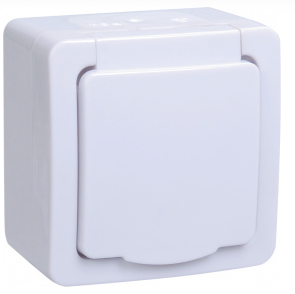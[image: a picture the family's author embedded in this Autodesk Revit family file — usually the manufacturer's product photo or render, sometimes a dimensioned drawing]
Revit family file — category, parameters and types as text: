
# Revit family: IEK_Розетка_ОУ_сЗК_сКР_16А_1мст_IP54_ГЕРМЕС_PLUS_белый
name_source: partatom
category: Электрические приборы
units: mm (PartAtom-declared; Revit-internal decimal feet)

## family parameters
Всегда вертикально = Да
На основе рабочей плоскости = Нет
Общий = Нет
При загрузке вырезать с полостями = Нет
Размер круглого соединителя = Использовать диаметр
Сохранять ориентацию аннотаций = Да
Тип детали = Нормальный
Точка расчета площади = Нет

## types (2) — shared parameters
ADSK_URL страницы изделия = https://qr.iek.group
ADSK_Версия Revit = v2019
ADSK_Версия семейства = 01.10.25
ADSK_Группирование = Электроустановочные изделия низковольтные
ADSK_Единица измерения = шт.
ADSK_Завод-изготовитель = IEK
ADSK_Количество фаз = 1
ADSK_Количество фаз числовое = 1
ADSK_Марка = ГЕРМЕС PLUS
ADSK_Материал = Цвет белый
ADSK_Материал наименование = Пластик
ADSK_Напряжение = 220 В
URL = https://www.iek.ru
Высота = 72 мм
Глубина = 52 мм
Изготовитель = IEK
Описание = Изделия серии "ГЕРМЕС PLUS" используются в помещениях с повышенной влажностью или запыленностью, а также под навесом на открытом воздухе.
Степень защиты = IP54
Тип монтажа = Поверхность монтажа (открытая установка)
Ширина = 72 мм

## per-type parameters (varying)
| type | ADSK_Код изделия | ADSK_Масса | ADSK_Наименование | ADSK_Наименование краткое | Материал крышки |
| РСб20-3-ГПБб | ERMP12-K01-16-54-EC | 0.12 | Розетка 1-местная для открытой установки РСб20-3-ГПБб с заземляющим контактом IP54 ГЕРМЕС PLUS (цвет крышки:белый) IEK | РСб20-3-ГПБ6 | Цвет белый |
| РСб20-3-ГПБд_КрышкаДымчатый | ERMP12-K03-16-54-EC | 0.115 | Розетка 1-местная для открытой установки РСб20-3-ГПБд с заземляющим контактом IP54 ГЕРМЕС PLUS (цвет крышки:дымчатый) IEK | РСб20-3-ГПБд | Цвет дымчатый |
